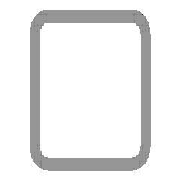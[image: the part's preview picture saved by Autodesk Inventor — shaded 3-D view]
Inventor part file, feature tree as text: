
AUTODESK INVENTOR PART (.ipt)
format: ipt  version: 2021 (Build 250183000, 183)  size: 144,384 bytes
history: native  units: mm (DEFAULTED — no unit token found)
features: other x5, sketch x3, extrude x1, split x1, plane x1
ambient origin geometry x8: Origin, YZ Plane, XZ Plane, XY Plane, X Axis, Y Axis, Z Axis, Center Point
bodies: Solid1 (feature_tree)
feature tree (11):
  parser-record x1  (decoder bookkeeping rows leaked as tree rows — omitted from the tree; the rows remain in map.json)
  other  "Driven Length"
  other  "Plano inicial"
  other  "Plano final"
  extrude  "Corpo"  TaperAngle=0.0deg  [1 undecoded]
  other  "Plano de trabalho4"
  split  "Dividir1"
  sketch  "Esboço"  dims[d11=50.8mm d12=4.7625mm d13=-15.698063mm d14=1000.0mm d15=25.4mm d16=25.4mm d17=9.525mm d18=90.0deg d19=1015.698063mm]
  sketch  "Sketch3"  dims[d3=1015.698063mm d4=0.0mm]
  plane  "Work Plane3"
  sketch  "Sketch4"  dims[d10=50.8mm]
note: 1 required parameter value undecoded (feature->parameter linkage not recoverable at this tier; creation-order binding heuristic only, values carry confidence <= 0.55)
